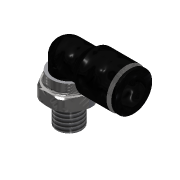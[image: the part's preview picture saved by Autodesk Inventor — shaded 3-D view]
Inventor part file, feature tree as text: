
AUTODESK INVENTOR PART (.ipt)
format: ipt  version: 2021 (Build 250183000, 183)  size: 266,752 bytes
history: native  units: in
note: dims shown in document units (in); Inventor stores cm internally (conversion verified against a paired STEP export)
features: extrude x2, sketch x2, thread x1
ambient origin geometry x8: Origin, YZ Plane, XZ Plane, XY Plane, X Axis, Y Axis, Z Axis, Center Point
bodies: Solid1 (feature_tree)
feature tree (5):
  extrude  "Extrusion1"  Depth=0.3937in
  extrude  "Extrusion2"  Depth=0.3937in TaperAngle=0.0deg
  thread  "Thread1"  [1 undecoded]
  sketch  "Sketch1"  dims[d0=0.3937in d1=0.0in d2=0.3937in]
  sketch  "Sketch2"  dims[d3=0.2756in d4=0.3937in d5=0.0in d6=0.3937in d7=0.0in]
note: 1 required parameter value undecoded (feature->parameter linkage not recoverable at this tier; creation-order binding heuristic only, values carry confidence <= 0.55)
